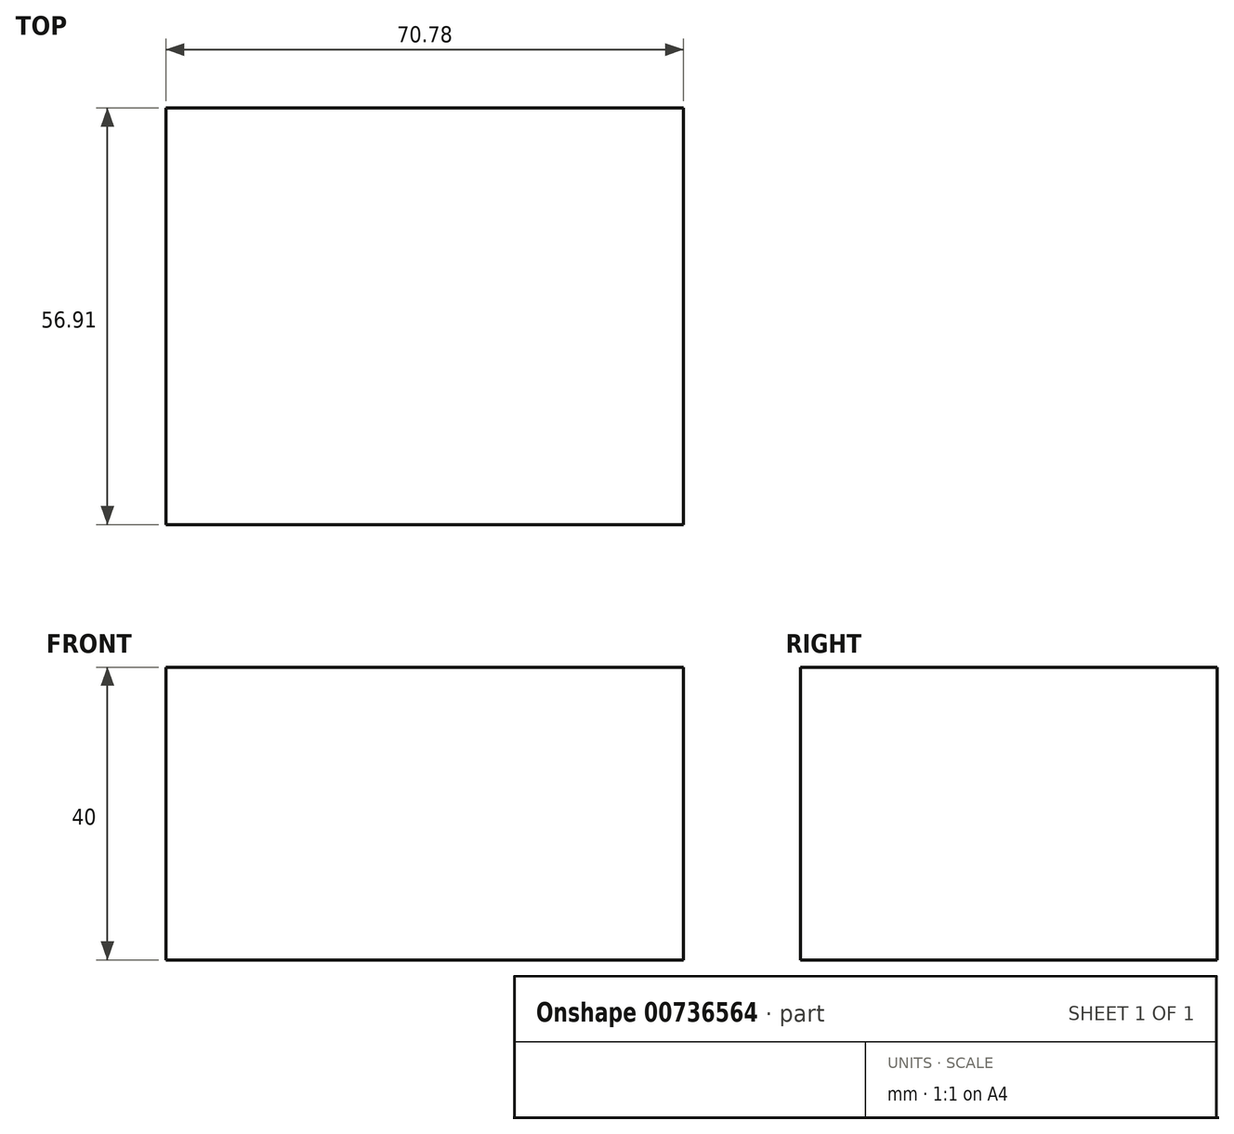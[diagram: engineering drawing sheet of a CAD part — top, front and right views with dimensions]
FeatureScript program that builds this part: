
annotation { "Feature Type Name" : "Feature", "Feature Type Description" : "" }
export const myFeature = defineFeature(function(context is Context, id is Id, definition is map)
    precondition{}
    {
        {
            var Q0;
            Q0=qCreatedBy(makeId("Top.planeOp"),FACE);
            var sketch = newSketch(context, id + "F0", { "sketchPlane" : qUnion([Q0])});
            skLineSegment(sketch, "E0.bottom", {"start": v(0, 0) * mm, "end": v(-70.78, 0) * mm});
            skLineSegment(sketch, "E0.top", {"start": v(0, 56.9) * mm, "end": v(-70.78, 56.9) * mm});
            skLineSegment(sketch, "E0.left", {"start": v(0, 0) * mm, "end": v(0, 56.9) * mm});
            skLineSegment(sketch, "E0.right", {"start": v(-70.78, 0) * mm, "end": v(-70.78, 56.9) * mm});
            skSolve(sketch);
        }
        {
            var Q0;
            Q0 = qSketchRegion(id + "F0", true);
            extrude(context, id + "F1", {"entities" : qUnion([Q0]), "depth" : 40 * mm, "offsetDistance" : 25.4 * mm});
        }
    });
